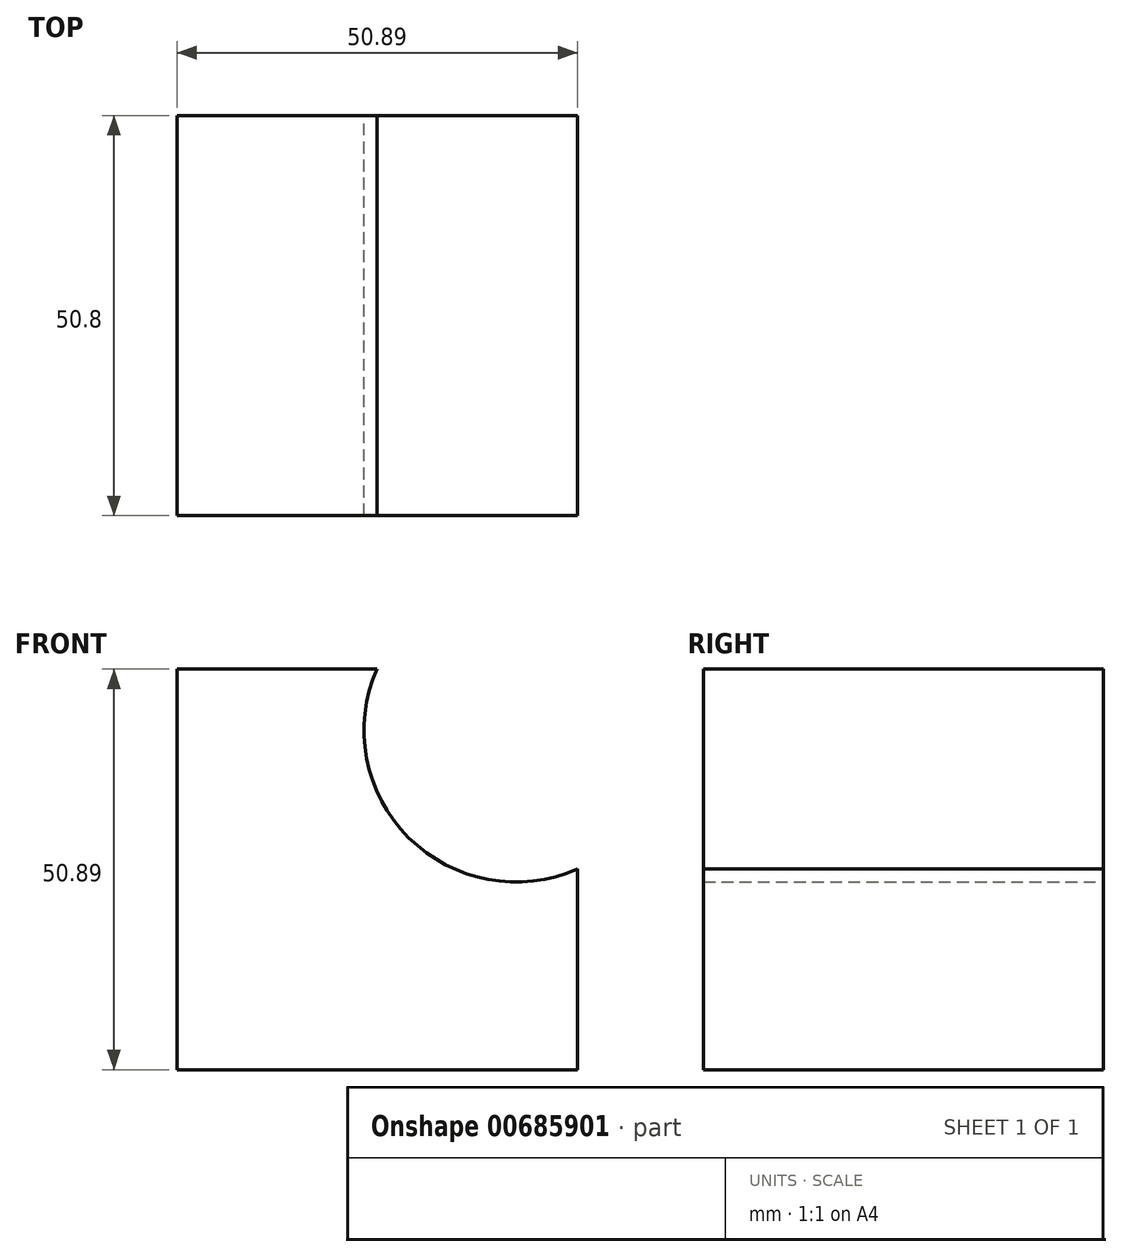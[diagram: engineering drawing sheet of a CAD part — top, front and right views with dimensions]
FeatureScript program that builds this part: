
annotation { "Feature Type Name" : "Feature", "Feature Type Description" : "" }
export const myFeature = defineFeature(function(context is Context, id is Id, definition is map)
    precondition{}
    {
        {
            var Q0;
            Q0=qCreatedBy(makeId("Front.planeOp"),FACE);
            var sketch = newSketch(context, id + "F0", { "sketchPlane" : qUnion([Q0])});
            skLineSegment(sketch, "E0", {"start": v(0, 0) * mm, "end": v(-50.89, 0) * mm});
            skLineSegment(sketch, "E1", {"start": v(-50.89, 0) * mm, "end": v(-50.89, 50.89) * mm});
            skLineSegment(sketch, "E2", {"start": v(-50.89, 50.89) * mm, "end": v(-25.5, 50.89) * mm});
            skLineSegment(sketch, "E3", {"start": v(0, 0) * mm, "end": v(0, 25.5) * mm});
            skArc(sketch, "E4", {"start": v(-25.5, 50.89) * mm, "mid": v(-21.43, 29.47) * mm, "end": v(0, 25.5) * mm});
            skSolve(sketch);
        }
        {
            var Q0;
            Q0 = qSketchRegion(id + "F0", true);
            extrude(context, id + "F1", {"entities" : qUnion([Q0]), "depth" : 50.8 * mm, "offsetDistance" : 25.4 * mm});
        }
    });
